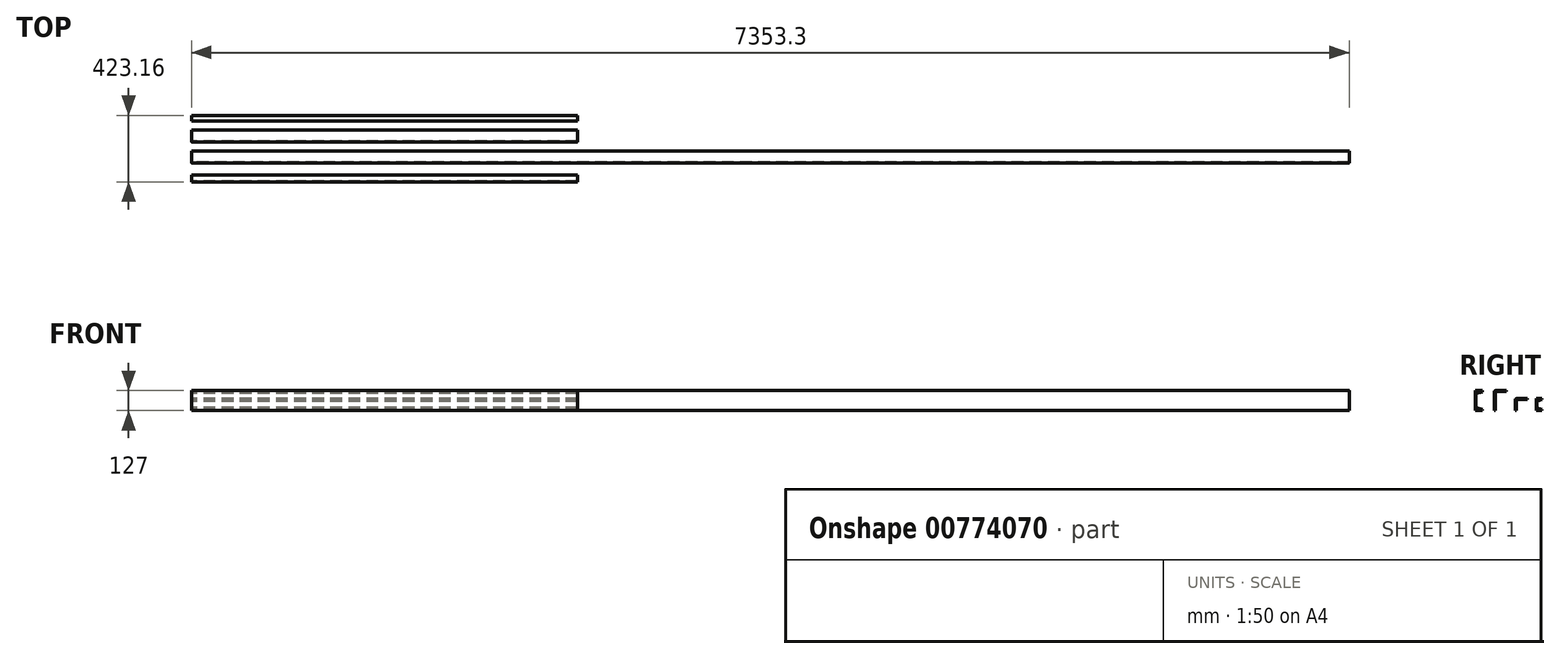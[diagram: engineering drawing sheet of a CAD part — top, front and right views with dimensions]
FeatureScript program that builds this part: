
annotation { "Feature Type Name" : "Feature", "Feature Type Description" : "" }
export const myFeature = defineFeature(function(context is Context, id is Id, definition is map)
    precondition{}
    {
        {
            var Q0;
            Q0=qCreatedBy(makeId("Right.planeOp"),FACE);
            var sketch = newSketch(context, id + "F0", { "sketchPlane" : qUnion([Q0])});
            skLineSegment(sketch, "E0", {"start": v(0, 0) * mm, "end": v(44.45, 0) * mm});
            skLineSegment(sketch, "E1", {"start": v(0, 0) * mm, "end": v(0, 127) * mm});
            skLineSegment(sketch, "E2", {"start": v(0, 127) * mm, "end": v(44.45, 127) * mm});
            skLineSegment(sketch, "E3", {"start": v(4.83, 107.95) * mm, "end": v(4.83, 19.05) * mm});
            skLineSegment(sketch, "E4", {"start": v(44.45, 0) * mm, "end": v(44.45, 8.13) * mm});
            skLineSegment(sketch, "E5", {"start": v(44.45, 8.13) * mm, "end": v(4.83, 19.05) * mm});
            skLineSegment(sketch, "E6", {"start": v(44.45, 127) * mm, "end": v(44.45, 118.87) * mm});
            skLineSegment(sketch, "E7", {"start": v(44.45, 118.87) * mm, "end": v(4.83, 107.95) * mm});
            skLineSegment(sketch, "E8", {"start": v(120.65, 0) * mm, "end": v(120.65, 117.48) * mm});
            skLineSegment(sketch, "E9", {"start": v(130.17, 127) * mm, "end": v(196.85, 127) * mm});
            skLineSegment(sketch, "E10", {"start": v(196.85, 127) * mm, "end": v(196.85, 120.65) * mm});
            skLineSegment(sketch, "E11", {"start": v(196.85, 120.65) * mm, "end": v(136.53, 120.65) * mm});
            skLineSegment(sketch, "E12", {"start": v(127, 111.12) * mm, "end": v(127, 0) * mm});
            skLineSegment(sketch, "E13", {"start": v(127, 0) * mm, "end": v(120.65, 0) * mm});
            skPoint(sketch, "E14.visualSharp", {"position": v(127, 120.65) * mm});
            skArc(sketch, "E14.filletArc", {"start": v(136.53, 120.65) * mm, "mid": v(129.79, 117.86) * mm, "end": v(127, 111.12) * mm});
            skPoint(sketch, "E15.visualSharp", {"position": v(120.65, 127) * mm});
            skArc(sketch, "E15.filletArc", {"start": v(130.17, 127) * mm, "mid": v(123.44, 124.21) * mm, "end": v(120.65, 117.48) * mm});
            skLineSegment(sketch, "E16", {"start": v(254, 0) * mm, "end": v(254, 66.67) * mm});
            skLineSegment(sketch, "E17", {"start": v(263.53, 76.2) * mm, "end": v(330.2, 76.2) * mm});
            skLineSegment(sketch, "E18", {"start": v(330.2, 76.2) * mm, "end": v(330.2, 69.85) * mm});
            skLineSegment(sketch, "E19", {"start": v(330.2, 69.85) * mm, "end": v(269.88, 69.85) * mm});
            skLineSegment(sketch, "E20", {"start": v(260.35, 60.32) * mm, "end": v(260.35, 0) * mm});
            skLineSegment(sketch, "E21", {"start": v(260.35, 0) * mm, "end": v(254, 0) * mm});
            skPoint(sketch, "E22.visualSharp", {"position": v(254, 76.2) * mm});
            skArc(sketch, "E22.filletArc", {"start": v(263.53, 76.2) * mm, "mid": v(256.79, 73.41) * mm, "end": v(254, 66.67) * mm});
            skPoint(sketch, "E23.visualSharp", {"position": v(260.35, 69.85) * mm});
            skArc(sketch, "E23.filletArc", {"start": v(269.88, 69.85) * mm, "mid": v(263.14, 67.06) * mm, "end": v(260.35, 60.32) * mm});
            skLineSegment(sketch, "E24", {"start": v(387.35, 0) * mm, "end": v(387.35, 76.2) * mm});
            skLineSegment(sketch, "E25", {"start": v(387.35, 76.2) * mm, "end": v(423.16, 76.2) * mm});
            skLineSegment(sketch, "E26", {"start": v(423.16, 76.2) * mm, "end": v(423.16, 69.27) * mm});
            skLineSegment(sketch, "E27", {"start": v(423.16, 69.27) * mm, "end": v(391.67, 58.74) * mm});
            skLineSegment(sketch, "E28", {"start": v(391.67, 58.74) * mm, "end": v(391.67, 17.46) * mm});
            skLineSegment(sketch, "E29", {"start": v(391.67, 17.46) * mm, "end": v(423.16, 6.93) * mm});
            skLineSegment(sketch, "E30", {"start": v(423.16, 6.93) * mm, "end": v(423.16, 0) * mm});
            skLineSegment(sketch, "E31", {"start": v(423.16, 0) * mm, "end": v(387.35, 0) * mm});
            skSolve(sketch);
        }
        {
            var Q0;
            Q0=makeQuery(id+"F0.imprint","IMPRINT",FACE,{"disambiguationData":[TD([[makeQuery(id+"F0.imprint","IMPRINT",EDGE,{"derivedFrom":sQuery(id+"F0.wireOp",EDGE,"E0")}),1.0]])]});
            extrude(context, id + "F1", {"entities" : qUnion([Q0]), "depth" : 2451.1 * mm, "offsetDistance" : 25.4 * mm});
        }
        {
            var Q0;
            Q0=makeQuery(id+"F0.imprint","IMPRINT",FACE,{"disambiguationData":[TD([[makeQuery(id+"F0.imprint","IMPRINT",EDGE,{"derivedFrom":sQuery(id+"F0.wireOp",EDGE,"E8")}),-1.0]])]});
            extrude(context, id + "F2", {"entities" : qUnion([Q0]), "depth" : 7353.3 * mm, "offsetDistance" : 25.4 * mm});
        }
        {
            var Q0;
            Q0=makeQuery(id+"F0.imprint","IMPRINT",FACE,{"disambiguationData":[TD([[makeQuery(id+"F0.imprint","IMPRINT",EDGE,{"derivedFrom":sQuery(id+"F0.wireOp",EDGE,"E16")}),-1.0]])]});
            extrude(context, id + "F3", {"entities" : qUnion([Q0]), "depth" : 2451.1 * mm, "offsetDistance" : 25.4 * mm});
        }
        {
            var Q0;
            Q0=makeQuery(id+"F0.imprint","IMPRINT",FACE,{"disambiguationData":[TD([[makeQuery(id+"F0.imprint","IMPRINT",EDGE,{"derivedFrom":sQuery(id+"F0.wireOp",EDGE,"E24")}),-1.0]])]});
            extrude(context, id + "F4", {"entities" : qUnion([Q0]), "depth" : 2451.1 * mm, "offsetDistance" : 25.4 * mm});
        }
    });
